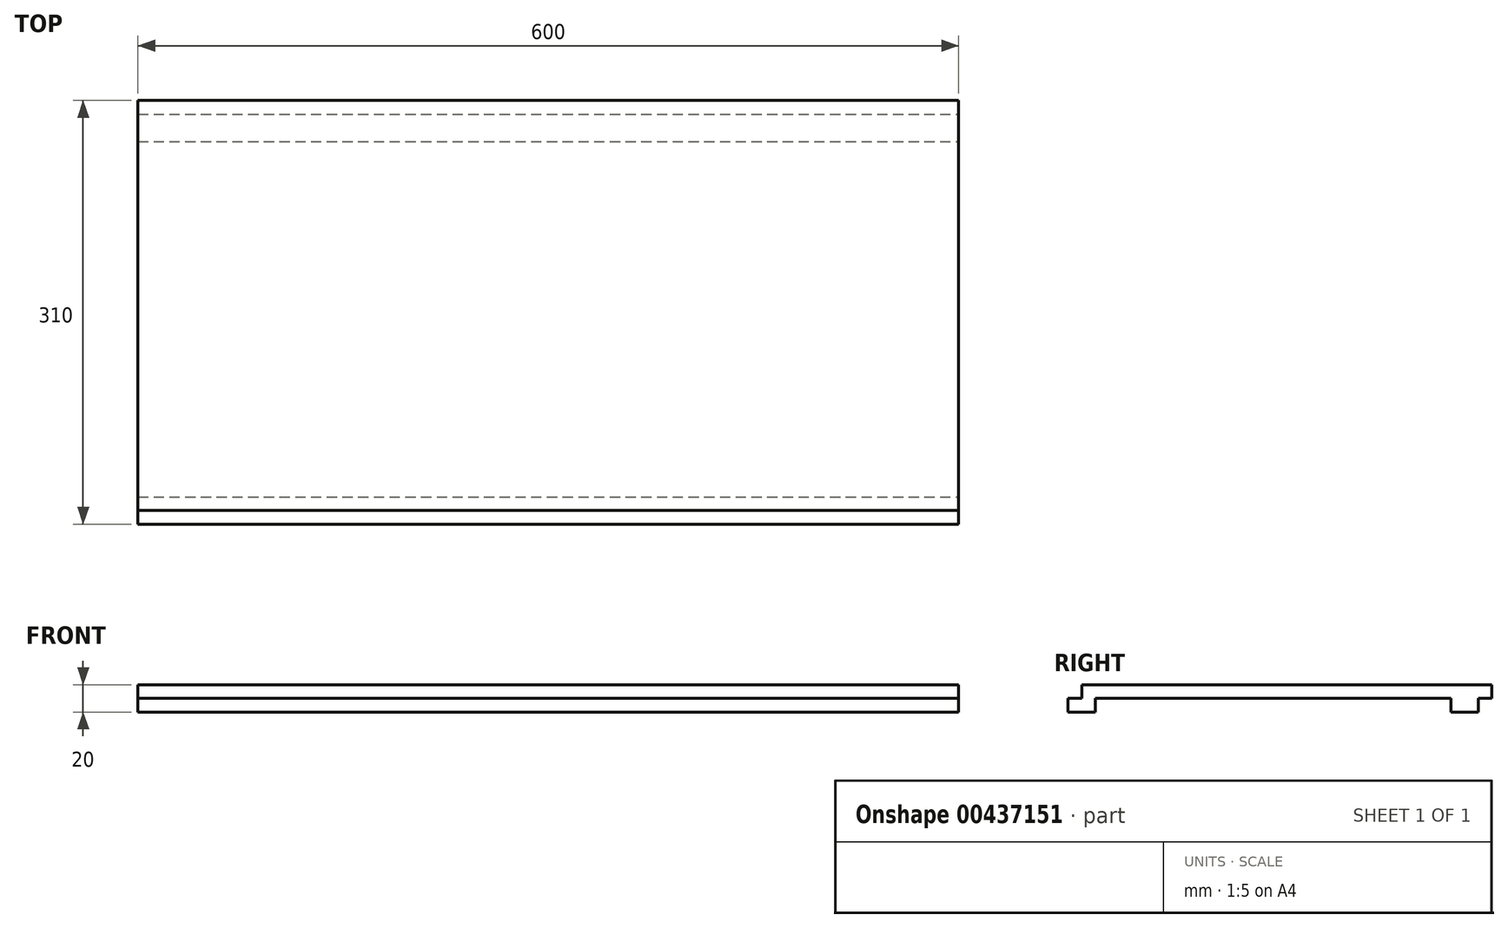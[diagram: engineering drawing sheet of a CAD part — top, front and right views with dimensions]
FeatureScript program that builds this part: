
annotation { "Feature Type Name" : "Feature", "Feature Type Description" : "" }
export const myFeature = defineFeature(function(context is Context, id is Id, definition is map)
    precondition{}
    {
        {
            var Q0;
            Q0=qCreatedBy(makeId("Top.planeOp"),FACE);
            var sketch = newSketch(context, id + "F0", { "sketchPlane" : qUnion([Q0])});
            skLineSegment(sketch, "E0.bottom", {"start": v(300, 150) * mm, "end": v(-300, 150) * mm});
            skLineSegment(sketch, "E0.top", {"start": v(300, -150) * mm, "end": v(-300, -150) * mm});
            skLineSegment(sketch, "E0.left", {"start": v(300, 150) * mm, "end": v(300, -150) * mm});
            skLineSegment(sketch, "E0.right", {"start": v(-300, 150) * mm, "end": v(-300, -150) * mm});
            skPoint(sketch, "E0.middle", {"position": v(0, 0) * mm});
            skLineSegment(sketch, "E1", {"start": v(-300, 0) * mm, "end": v(300, 0) * mm, "construction": true});
            skSolve(sketch);
        }
        {
            var Q0;
            Q0=makeQuery(id+"F0.imprint","IMPRINT",FACE,{"disambiguationData":[TD([[makeQuery(id+"F0.imprint","IMPRINT",EDGE,{"derivedFrom":sQuery(id+"F0.wireOp",EDGE,"E0.bottom")}),1.0]])]});
            extrude(context, id + "F1", {"entities" : qUnion([Q0]), "depth" : 10 * mm});
        }
        {
            var Q0;
            Q0=makeQuery(id+"F0.imprint","IMPRINT",FACE,{"disambiguationData":[TD([[makeQuery(id+"F0.imprint","IMPRINT",EDGE,{"derivedFrom":sQuery(id+"F0.wireOp",EDGE,"E0.bottom")}),1.0]])]});
            var sketch = newSketch(context, id + "F2", { "sketchPlane" : qUnion([Q0])});
            skLineSegment(sketch, "E2.0", {"start": v(-300, 150) * mm, "end": v(-300, -150) * mm, "construction": true});
            skLineSegment(sketch, "E3.0", {"start": v(300, 150) * mm, "end": v(300, -150) * mm, "construction": true});
            skLineSegment(sketch, "E4.0", {"start": v(300, -150) * mm, "end": v(-300, -150) * mm, "construction": true});
            skLineSegment(sketch, "E5.0", {"start": v(300, 150) * mm, "end": v(-300, 150) * mm, "construction": true});
            skLineSegment(sketch, "E6.bottom", {"start": v(-300, 140) * mm, "end": v(300, 140) * mm});
            skLineSegment(sketch, "E6.top", {"start": v(-300, 120) * mm, "end": v(300, 120) * mm});
            skLineSegment(sketch, "E6.left", {"start": v(-300, 140) * mm, "end": v(-300, 120) * mm});
            skLineSegment(sketch, "E6.right", {"start": v(300, 140) * mm, "end": v(300, 120) * mm});
            skLineSegment(sketch, "E7.bottom", {"start": v(-300, -140) * mm, "end": v(300, -140) * mm});
            skLineSegment(sketch, "E7.top", {"start": v(-300, -160) * mm, "end": v(300, -160) * mm});
            skLineSegment(sketch, "E7.left", {"start": v(-300, -140) * mm, "end": v(-300, -160) * mm});
            skLineSegment(sketch, "E7.right", {"start": v(300, -140) * mm, "end": v(300, -160) * mm});
            skSolve(sketch);
        }
        {
            var Q0;
            {var subQ0=sQuery(id+"F2.wireOp",EDGE,"E7.bottom");Q0=makeQuery(id+"F2.imprint","IMPRINT",FACE,{"disambiguationData":[TD([[makeQuery(id+"F2.imprint","IMPRINT",EDGE,{"derivedFrom":subQ0}),-1.0]])]});}
            var Q1;
            {var subQ0=sQuery(id+"F2.wireOp",EDGE,"E7.top");Q1=makeQuery(id+"F2.imprint","IMPRINT",FACE,{"disambiguationData":[TD([[makeQuery(id+"F2.imprint","IMPRINT",EDGE,{"derivedFrom":subQ0}),1.0]])]});}
            var Q2;
            Q2=makeQuery(id+"F2.imprint","IMPRINT",FACE,{"disambiguationData":[TD([[makeQuery(id+"F2.imprint","IMPRINT",EDGE,{"derivedFrom":sQuery(id+"F2.wireOp",EDGE,"E6.bottom")}),-1.0]])]});
            extrude(context, id + "F3", {"entities" : qUnion([Q0, Q1, Q2]), "operationType" : NewBodyOperationType.ADD, "oppositeDirection" : true, "depth" : 10 * mm});
        }
    });
